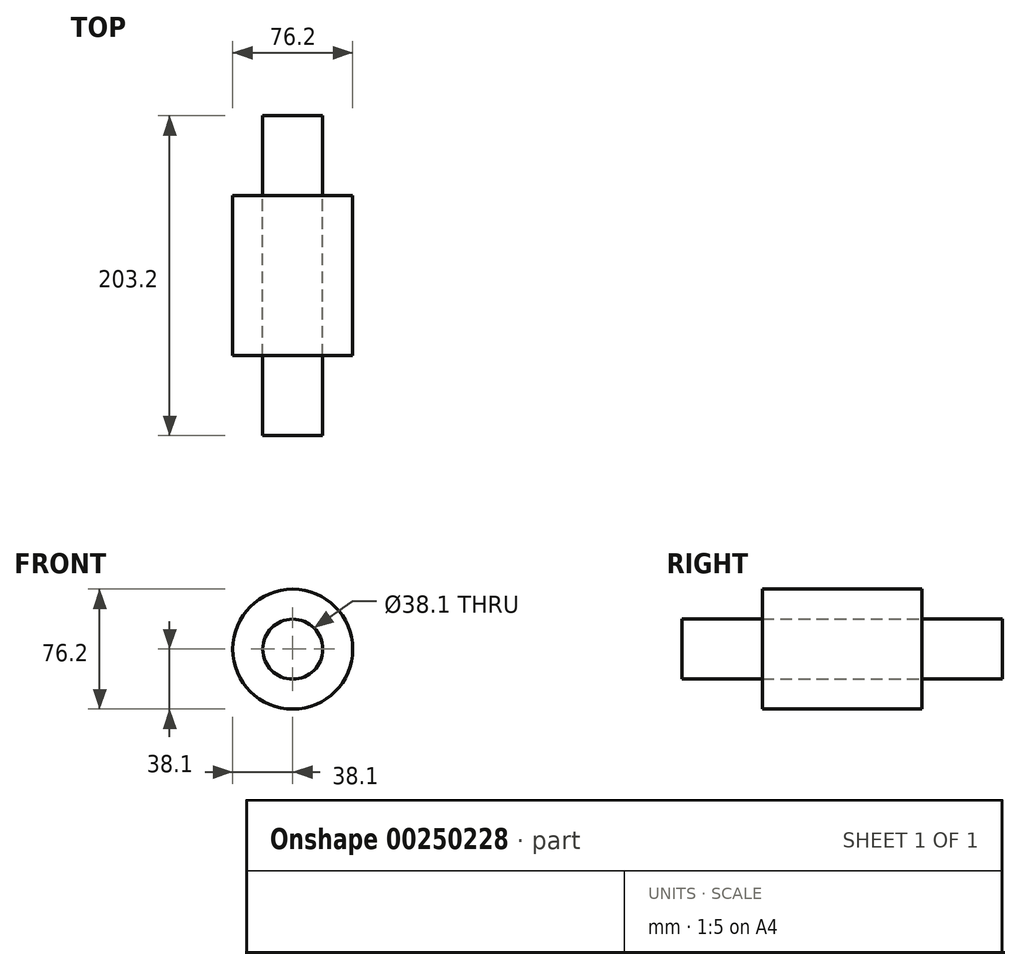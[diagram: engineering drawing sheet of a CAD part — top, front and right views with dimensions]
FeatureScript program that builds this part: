
annotation { "Feature Type Name" : "Feature", "Feature Type Description" : "" }
export const myFeature = defineFeature(function(context is Context, id is Id, definition is map)
    precondition{}
    {
        {
            var Q0;
            Q0=qCreatedBy(makeId("Front.planeOp"),FACE);
            var sketch = newSketch(context, id + "F0", { "sketchPlane" : qUnion([Q0])});
            skCircle(sketch, "E0", {"center": v(0, 0) * mm, "radius": 38.1 * mm});
            skCircle(sketch, "E1", {"center": v(0, 0) * mm, "radius": 19.05 * mm});
            skSolve(sketch);
        }
        {
            var Q0;
            Q0 = qSketchRegion(id + "F0", true);
            extrude(context, id + "F1", {"entities" : qUnion([Q0]), "endBound" : BoundingType.SYMMETRIC, "depth" : 101.6 * mm});
        }
        {
            var Q0;
            Q0=makeQuery(id+"F0.imprint","IMPRINT",FACE,{"disambiguationData":[TD([[makeQuery(id+"F0.imprint","IMPRINT",EDGE,{"derivedFrom":sQuery(id+"F0.wireOp",EDGE,"E1")}),1.0]])]});
            extrude(context, id + "F2", {"entities" : qUnion([Q0]), "endBound" : BoundingType.SYMMETRIC, "depth" : 203.2 * mm});
        }
    });
